# Revit family: PRE080028-FR
name_source: partatom
category: Appareils sanitaires
revit_build: Autodesk Revit 2017 (Build: 20160225_1515(x64)
units: mm (PartAtom-declared; Revit-internal decimal feet)

## family parameters
Basée sur le plan de construction = Non
Cote de connecteur circulaire = Utiliser le diamètre
Couper avec des vides une fois chargée = Non
Partagée = Non
Point de calcul de pièce = Non
Toujours verticalement = Oui
Type d'élément = Normal

## types (1)
- 70832 PRESTO CHEF Mitigeur monocommande sur plage avec bec par-dessus
    Adresse = 7, RUE RACINE - 92542 MONTROUGE CEDEX FRANCE
    Debit = 1,9l/min avec limiteur de débit intégré
 (sprayer)
 Dispositif anti-coup de bélier

 Brise-jet : anti-vandalisme et anti-bouchage
    Description = le bec est caché sous le comptoir : plus esthétique
déport de la manette sur le côté : accès facilité pour le lavage
Produit résistant à un usage intensif
Interface corps/bec renforcé avec double paliers de glissement : absence de jeu et endurance élevée
Bec cossu : Ø 22 mm - épaisseur 1,5mm
Commande ergonomique et robuste : facilité de préhension
Hygiène : bec à intérieur lisse
Facilité de nettoyage
Facilité de maintenance : disponibilité de toutes les pièces d'usure
Brise-jet pour canaliser l'eau et éviter les projections d'eau latérales
    Diamètre Nominal = 15 mm  [stored 0.0492126 ft]
    Edition number = 0
    Fabricant = LES ROBINETS PRESTO S.A.
    Finition = Corps en laiton chromé conforme aux normes NF EN1982/ NF EN 12164 / NF EN 12165
Traitement de surface Nickel-Chrome selon NF EN12540
Résistance au brouillard salin neutre (NSS) : 200 h selon NF ISO 9242
    Flux = 0.0 L/s
    Fonction = Bec orientable à 360° Saillie 250 mm Hauteur sous bec 146 mm - diamètre 22 mm
Epaisseur de bec : 1,5 mm
Cartouche céramique avec débit 20 L/min à 3 bar
Brise-jet anti-tartre interchangeable

Pression d'utilisation recommandée : 1 à 5 bars

Débit : 20L/min à 3 bar

Alimentation hydraulique : G 1/2'' (15x 21)

Matière et couleur de finition :
Corps et bec en laiton chromé
Matière conforme avec la liste "UBA"

Résistance thermique : Résiste à une température de 75° C durant 30 minutes (dans le cadre de chocs thermiques).

Livré avec :
1 étrier de fixation
2 flexibles PEX avec écrou femelle tresse en acier inoxydable G1/2'' Lg 660 mm avec clapets anti-retour NF
2 filtres

Option : Possibilité d'ajouter une réhausse vendue séparément, facilitant le passage de gros contenants
    Hauteur = 237 mm  [stored 0.777559 ft]
    LC = 15 mm  [stored 0.0492126 ft]
    Largeur = 128 mm  [stored 0.419948 ft]
    Lien CCTP = http://www.prestodatashare.com
    Lien fiche produit = http://www.prestodatashare.com
    Lien notice d'utilisation = http://www.prestodatashare.com
    Matériau = Laiton poli chromé
    Modèle = 70832 PRESTO CHEF Mitigeur monocommande sur plage avec bec par-dessus
    PC = 30 mm  [stored 0.0984252 ft]
    Perte de charge = 0.0 Pa
    Polantis code = PRE080028
    Product Guid = 000211d8-50d9-4629-b294-d35f99251844
    Product data url = https://www.bimobject.com
    Profondeur = 286 mm  [stored 0.93832 ft]
    Raccordement = 2xG1/2 couplé dessous arrière gauche
    Reference = 70832
    URL = http://www.prestodatashare.com
    URL Fabricant = http://www.prestodatashare.com
    Variantes = 70832

note: [stored X ft] marks values corroborated as IEEE doubles in the binary element streams (Revit-internal decimal feet)
